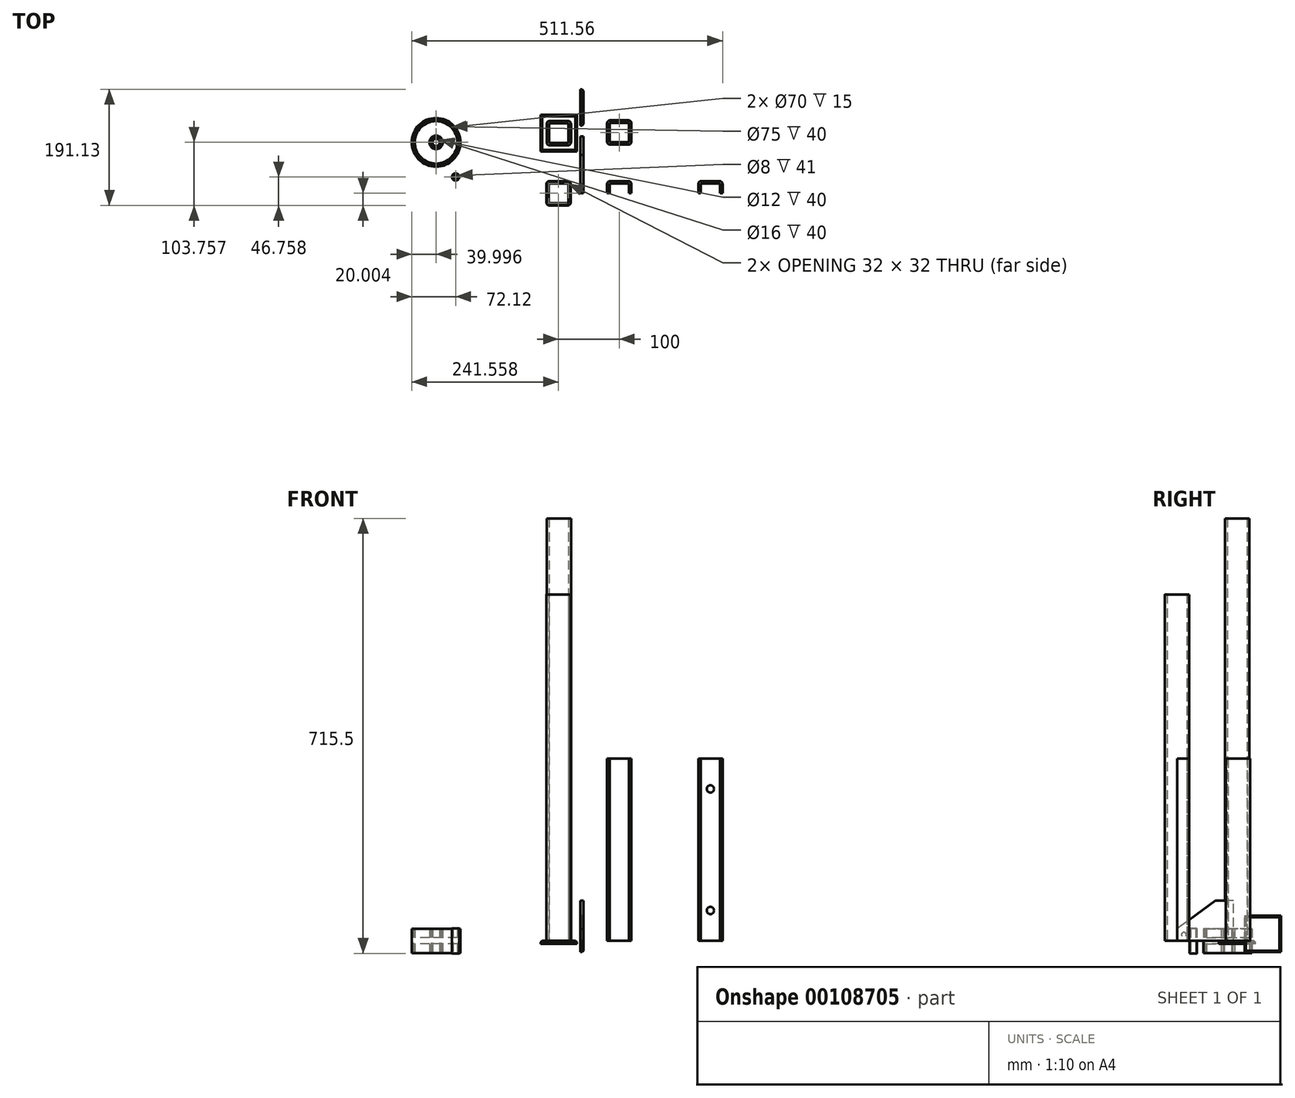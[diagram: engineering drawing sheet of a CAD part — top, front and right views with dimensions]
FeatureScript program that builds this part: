
annotation { "Feature Type Name" : "Feature", "Feature Type Description" : "" }
export const myFeature = defineFeature(function(context is Context, id is Id, definition is map)
    precondition{}
    {
        {
            var Q0;
            Q0=qCreatedBy(makeId("Top.planeOp"),FACE);
            var sketch = newSketch(context, id + "F0", { "sketchPlane" : qUnion([Q0])});
            skLineSegment(sketch, "E0.bottom", {"start": v(-50.42, 65.64) * mm, "end": v(-20.42, 65.64) * mm});
            skLineSegment(sketch, "E0.top", {"start": v(-50.42, 25.64) * mm, "end": v(-20.42, 25.64) * mm});
            skLineSegment(sketch, "E0.left", {"start": v(-55.42, 60.64) * mm, "end": v(-55.42, 30.64) * mm});
            skLineSegment(sketch, "E0.right", {"start": v(-15.42, 60.64) * mm, "end": v(-15.42, 30.64) * mm});
            skLineSegment(sketch, "E1.0", {"start": v(-51.42, 60.64) * mm, "end": v(-51.42, 30.64) * mm});
            skLineSegment(sketch, "E1.1", {"start": v(-50.42, 61.64) * mm, "end": v(-20.42, 61.64) * mm});
            skLineSegment(sketch, "E1.2", {"start": v(-19.42, 60.64) * mm, "end": v(-19.42, 30.64) * mm});
            skLineSegment(sketch, "E1.3", {"start": v(-50.42, 29.64) * mm, "end": v(-20.42, 29.64) * mm});
            skPoint(sketch, "E2.visualSharp", {"position": v(-51.42, 61.64) * mm});
            skArc(sketch, "E2.filletArc", {"start": v(-50.42, 61.64) * mm, "mid": v(-51.13, 61.35) * mm, "end": v(-51.42, 60.64) * mm});
            skPoint(sketch, "E3.visualSharp", {"position": v(-19.42, 61.64) * mm});
            skArc(sketch, "E3.filletArc", {"start": v(-19.42, 60.64) * mm, "mid": v(-19.71, 61.35) * mm, "end": v(-20.42, 61.64) * mm});
            skPoint(sketch, "E4.visualSharp", {"position": v(-19.42, 29.64) * mm});
            skArc(sketch, "E4.filletArc", {"start": v(-20.42, 29.64) * mm, "mid": v(-19.71, 29.93) * mm, "end": v(-19.42, 30.64) * mm});
            skPoint(sketch, "E5.visualSharp", {"position": v(-51.42, 29.64) * mm});
            skArc(sketch, "E5.filletArc", {"start": v(-51.42, 30.64) * mm, "mid": v(-51.13, 29.93) * mm, "end": v(-50.42, 29.64) * mm});
            skPoint(sketch, "E6.visualSharp", {"position": v(-55.42, 65.64) * mm});
            skArc(sketch, "E6.filletArc", {"start": v(-50.42, 65.64) * mm, "mid": v(-53.96, 64.17) * mm, "end": v(-55.42, 60.64) * mm});
            skPoint(sketch, "E7.visualSharp", {"position": v(-15.42, 65.64) * mm});
            skArc(sketch, "E7.filletArc", {"start": v(-15.42, 60.64) * mm, "mid": v(-16.88, 64.17) * mm, "end": v(-20.42, 65.64) * mm});
            skPoint(sketch, "E8.visualSharp", {"position": v(-15.42, 25.64) * mm});
            skArc(sketch, "E8.filletArc", {"start": v(-20.42, 25.64) * mm, "mid": v(-16.88, 27.1) * mm, "end": v(-15.42, 30.64) * mm});
            skLineSegment(sketch, "E9.0.1.0", {"start": v(-50.9, -69.37) * mm, "end": v(-20.9, -69.37) * mm});
            skLineSegment(sketch, "E9.0.1.1", {"start": v(-19.9, -38.37) * mm, "end": v(-19.9, -68.37) * mm});
            skPoint(sketch, "E9.0.1.2", {"position": v(-19.9, -37.37) * mm});
            skLineSegment(sketch, "E9.0.1.3", {"start": v(-50.9, -37.37) * mm, "end": v(-20.9, -37.37) * mm});
            skLineSegment(sketch, "E9.0.1.4", {"start": v(-50.9, -33.37) * mm, "end": v(-20.9, -33.37) * mm});
            skPoint(sketch, "E9.0.1.5", {"position": v(-51.9, -69.37) * mm});
            skPoint(sketch, "E9.0.1.6", {"position": v(-51.9, -37.37) * mm});
            skLineSegment(sketch, "E9.0.1.7", {"start": v(-50.9, -73.37) * mm, "end": v(-20.9, -73.37) * mm});
            skPoint(sketch, "E9.0.1.8", {"position": v(-19.9, -69.37) * mm});
            skLineSegment(sketch, "E9.0.1.9", {"start": v(-51.9, -38.37) * mm, "end": v(-51.9, -68.37) * mm});
            skLineSegment(sketch, "E9.0.1.10", {"start": v(-55.9, -38.37) * mm, "end": v(-55.9, -68.37) * mm});
            skLineSegment(sketch, "E9.0.1.11", {"start": v(-15.9, -38.37) * mm, "end": v(-15.9, -68.37) * mm});
            skPoint(sketch, "E9.0.1.12", {"position": v(-55.9, -33.37) * mm});
            skPoint(sketch, "E9.0.1.13", {"position": v(-15.9, -33.37) * mm});
            skPoint(sketch, "E9.0.1.14", {"position": v(-15.9, -73.37) * mm});
            skArc(sketch, "E9.0.1.15", {"start": v(-50.9, -33.37) * mm, "mid": v(-54.43, -34.83) * mm, "end": v(-55.9, -38.37) * mm});
            skArc(sketch, "E9.0.1.16", {"start": v(-20.9, -73.37) * mm, "mid": v(-17.36, -71.9) * mm, "end": v(-15.9, -68.37) * mm});
            skArc(sketch, "E9.0.1.17", {"start": v(-15.9, -38.37) * mm, "mid": v(-17.36, -34.83) * mm, "end": v(-20.9, -33.37) * mm});
            skArc(sketch, "E9.0.1.18", {"start": v(-19.9, -38.37) * mm, "mid": v(-20.19, -37.66) * mm, "end": v(-20.9, -37.37) * mm});
            skArc(sketch, "E9.0.1.19", {"start": v(-51.9, -68.37) * mm, "mid": v(-51.6, -69.07) * mm, "end": v(-50.9, -69.37) * mm});
            skArc(sketch, "E9.0.1.20", {"start": v(-50.9, -37.37) * mm, "mid": v(-51.6, -37.66) * mm, "end": v(-51.9, -38.37) * mm});
            skArc(sketch, "E9.0.1.21", {"start": v(-20.9, -69.37) * mm, "mid": v(-20.19, -69.07) * mm, "end": v(-19.9, -68.37) * mm});
            skLineSegment(sketch, "E9.1.0.0", {"start": v(49.1, 30.63) * mm, "end": v(79.1, 30.63) * mm});
            skLineSegment(sketch, "E9.1.0.1", {"start": v(80.1, 61.63) * mm, "end": v(80.1, 31.63) * mm});
            skPoint(sketch, "E9.1.0.2", {"position": v(80.1, 62.63) * mm});
            skLineSegment(sketch, "E9.1.0.3", {"start": v(49.1, 62.63) * mm, "end": v(79.1, 62.63) * mm});
            skLineSegment(sketch, "E9.1.0.4", {"start": v(49.1, 66.63) * mm, "end": v(79.1, 66.63) * mm});
            skPoint(sketch, "E9.1.0.5", {"position": v(48.1, 30.63) * mm});
            skPoint(sketch, "E9.1.0.6", {"position": v(48.1, 62.63) * mm});
            skLineSegment(sketch, "E9.1.0.7", {"start": v(49.1, 26.63) * mm, "end": v(79.1, 26.63) * mm});
            skPoint(sketch, "E9.1.0.8", {"position": v(80.1, 30.63) * mm});
            skLineSegment(sketch, "E9.1.0.9", {"start": v(48.1, 61.63) * mm, "end": v(48.1, 31.63) * mm});
            skLineSegment(sketch, "E9.1.0.10", {"start": v(44.1, 61.63) * mm, "end": v(44.1, 31.63) * mm});
            skLineSegment(sketch, "E9.1.0.11", {"start": v(84.1, 61.63) * mm, "end": v(84.1, 31.63) * mm});
            skPoint(sketch, "E9.1.0.12", {"position": v(44.1, 66.63) * mm});
            skPoint(sketch, "E9.1.0.13", {"position": v(84.1, 66.63) * mm});
            skPoint(sketch, "E9.1.0.14", {"position": v(84.1, 26.63) * mm});
            skArc(sketch, "E9.1.0.15", {"start": v(49.1, 66.63) * mm, "mid": v(45.57, 65.17) * mm, "end": v(44.1, 61.63) * mm});
            skArc(sketch, "E9.1.0.16", {"start": v(79.1, 26.63) * mm, "mid": v(82.64, 28.1) * mm, "end": v(84.1, 31.63) * mm});
            skArc(sketch, "E9.1.0.17", {"start": v(84.1, 61.63) * mm, "mid": v(82.64, 65.17) * mm, "end": v(79.1, 66.63) * mm});
            skArc(sketch, "E9.1.0.18", {"start": v(80.1, 61.63) * mm, "mid": v(79.81, 62.34) * mm, "end": v(79.1, 62.63) * mm});
            skArc(sketch, "E9.1.0.19", {"start": v(48.1, 31.63) * mm, "mid": v(48.4, 30.93) * mm, "end": v(49.1, 30.63) * mm});
            skArc(sketch, "E9.1.0.20", {"start": v(49.1, 62.63) * mm, "mid": v(48.4, 62.34) * mm, "end": v(48.1, 61.63) * mm});
            skArc(sketch, "E9.1.0.21", {"start": v(79.1, 30.63) * mm, "mid": v(79.81, 30.93) * mm, "end": v(80.1, 31.63) * mm});
            skPoint(sketch, "E9.1.1.2", {"position": v(80.1, -37.37) * mm});
            skLineSegment(sketch, "E9.1.1.3", {"start": v(49.1, -37.37) * mm, "end": v(79.1, -37.37) * mm});
            skLineSegment(sketch, "E9.1.1.4", {"start": v(49.1, -33.37) * mm, "end": v(79.1, -33.37) * mm});
            skPoint(sketch, "E9.1.1.6", {"position": v(48.1, -37.37) * mm});
            skLineSegment(sketch, "E9.1.1.9", {"start": v(48.1, -38.37) * mm, "end": v(48.1, -53.37) * mm});
            skPoint(sketch, "E9.1.1.12", {"position": v(44.1, -33.37) * mm});
            skPoint(sketch, "E9.1.1.13", {"position": v(84.1, -33.37) * mm});
            skArc(sketch, "E9.1.1.15", {"start": v(49.1, -33.37) * mm, "mid": v(45.57, -34.83) * mm, "end": v(44.1, -38.37) * mm});
            skArc(sketch, "E9.1.1.17", {"start": v(84.1, -38.37) * mm, "mid": v(82.64, -34.83) * mm, "end": v(79.1, -33.37) * mm});
            skArc(sketch, "E9.1.1.18", {"start": v(80.1, -38.37) * mm, "mid": v(79.81, -37.66) * mm, "end": v(79.1, -37.37) * mm});
            skArc(sketch, "E9.1.1.20", {"start": v(49.1, -37.37) * mm, "mid": v(48.4, -37.66) * mm, "end": v(48.1, -38.37) * mm});
            skPoint(sketch, "E10.visualSharp", {"position": v(-55.42, 25.64) * mm});
            skArc(sketch, "E10.filletArc", {"start": v(-55.42, 30.64) * mm, "mid": v(-53.96, 27.1) * mm, "end": v(-50.42, 25.64) * mm});
            skPoint(sketch, "E11.visualSharp", {"position": v(44.1, 26.63) * mm});
            skArc(sketch, "E11.filletArc", {"start": v(44.1, 31.63) * mm, "mid": v(45.57, 28.1) * mm, "end": v(49.1, 26.63) * mm});
            skPoint(sketch, "E12.visualSharp", {"position": v(-55.9, -73.37) * mm});
            skArc(sketch, "E12.filletArc", {"start": v(-55.9, -68.37) * mm, "mid": v(-54.43, -71.9) * mm, "end": v(-50.9, -73.37) * mm});
            skLineSegment(sketch, "E13", {"start": v(44.1, -53.37) * mm, "end": v(44.1, -38.37) * mm});
            skLineSegment(sketch, "E14", {"start": v(84.1, -38.37) * mm, "end": v(84.1, -53.37) * mm});
            skLineSegment(sketch, "E15", {"start": v(80.1, -38.37) * mm, "end": v(80.1, -53.37) * mm});
            skLineSegment(sketch, "E16", {"start": v(44.1, -53.37) * mm, "end": v(48.1, -53.37) * mm});
            skLineSegment(sketch, "E17", {"start": v(80.1, -53.37) * mm, "end": v(84.1, -53.37) * mm});
            skLineSegment(sketch, "E18.0", {"start": v(-20.42, 60.64) * mm, "end": v(-20.42, 30.64) * mm});
            skLineSegment(sketch, "E18.1", {"start": v(-50.42, 60.64) * mm, "end": v(-20.42, 60.64) * mm});
            skLineSegment(sketch, "E18.2", {"start": v(-50.42, 60.64) * mm, "end": v(-50.42, 30.64) * mm});
            skLineSegment(sketch, "E18.3", {"start": v(-50.42, 30.64) * mm, "end": v(-20.42, 30.64) * mm});
            skLineSegment(sketch, "E19.bottom", {"start": v(-65.42, 75.64) * mm, "end": v(-5.42, 75.64) * mm});
            skLineSegment(sketch, "E19.top", {"start": v(-65.42, 15.64) * mm, "end": v(-5.42, 15.64) * mm});
            skLineSegment(sketch, "E19.left", {"start": v(-65.42, 75.64) * mm, "end": v(-65.42, 15.64) * mm});
            skLineSegment(sketch, "E19.right", {"start": v(-5.42, 75.64) * mm, "end": v(-5.42, 15.64) * mm});
            skPoint(sketch, "E19.middle", {"position": v(-35.42, 45.64) * mm});
            skPoint(sketch, "E19.middle.positionSnap0", {"position": v(-20.42, 45.64) * mm});
            skPoint(sketch, "E19.middle.positionSnap1", {"position": v(-35.42, 30.64) * mm});
            skPoint(sketch, "E19.centerSnap0", {"position": v(-20.42, 45.64) * mm});
            skPoint(sketch, "E19.centerSnap1", {"position": v(-35.42, 30.64) * mm});
            skSolve(sketch);
        }
        {
            var Q0;
            Q0=qCreatedBy(makeId("Right.planeOp"),FACE);
            var sketch = newSketch(context, id + "F1", { "sketchPlane" : qUnion([Q0])});
            skLineSegment(sketch, "E20", {"start": v(-53.07, 0) * mm, "end": v(39.93, 0) * mm});
            skLineSegment(sketch, "E21", {"start": v(39.93, 0) * mm, "end": v(39.93, 66) * mm});
            skLineSegment(sketch, "E22", {"start": v(39.93, 66) * mm, "end": v(9.93, 66) * mm});
            skLineSegment(sketch, "E23", {"start": v(9.93, 66) * mm, "end": v(-53.07, 20.01) * mm});
            skLineSegment(sketch, "E24", {"start": v(-53.07, 20.01) * mm, "end": v(-53.07, 0) * mm});
            skLineSegment(sketch, "E25.bottom", {"start": v(57.76, 41.49) * mm, "end": v(117.76, 41.49) * mm});
            skLineSegment(sketch, "E25.top", {"start": v(57.76, -18.51) * mm, "end": v(117.76, -18.51) * mm});
            skLineSegment(sketch, "E25.left", {"start": v(57.76, 41.49) * mm, "end": v(57.76, -18.51) * mm});
            skLineSegment(sketch, "E25.right", {"start": v(117.76, 41.49) * mm, "end": v(117.76, -18.51) * mm});
            skCircle(sketch, "E26", {"center": v(-42.07, 10) * mm, "radius": 4 * mm});
            skSolve(sketch);
        }
        {
            var Q0;
            Q0=makeQuery(id+"F0.imprint","IMPRINT",FACE,{"disambiguationData":[TD([[makeQuery(id+"F0.imprint","IMPRINT",EDGE,{"derivedFrom":sQuery(id+"F0.wireOp",EDGE,"E0.bottom")}),-1.0]])]});
            extrude(context, id + "F2", {"entities" : qUnion([Q0]), "depth" : 695 * mm});
        }
        {
            var Q0;
            Q0=makeQuery(id+"F0.imprint","IMPRINT",FACE,{"disambiguationData":[TD([[makeQuery(id+"F0.imprint","IMPRINT",EDGE,{"derivedFrom":sQuery(id+"F0.wireOp",EDGE,"E9.0.1.0")}),-1.0]])]});
            extrude(context, id + "F3", {"entities" : qUnion([Q0]), "depth" : 570 * mm});
        }
        {
            var Q0;
            Q0=makeQuery(id+"F0.imprint","IMPRINT",FACE,{"disambiguationData":[TD([[makeQuery(id+"F0.imprint","IMPRINT",EDGE,{"derivedFrom":sQuery(id+"F0.wireOp",EDGE,"E9.1.0.0")}),-1.0]])]});
            extrude(context, id + "F4", {"entities" : qUnion([Q0]), "depth" : 300 * mm});
        }
        {
            var Q0;
            Q0=makeQuery(id+"F0.imprint","IMPRINT",FACE,{"disambiguationData":[TD([[makeQuery(id+"F0.imprint","IMPRINT",EDGE,{"derivedFrom":sQuery(id+"F0.wireOp",EDGE,"E9.1.1.3")}),1.0]])]});
            extrude(context, id + "F5", {"entities" : qUnion([Q0]), "depth" : 300 * mm});
        }
        {
            var Q0;
            Q0=makeQuery(id+"F1.imprint","IMPRINT",FACE,{"disambiguationData":[TD([[makeQuery(id+"F1.imprint","IMPRINT",EDGE,{"derivedFrom":sQuery(id+"F1.wireOp",EDGE,"E20")}),1.0]])]});
            var Q1;
            Q1=makeQuery(id+"F1.imprint","IMPRINT",FACE,{"disambiguationData":[TD([[makeQuery(id+"F1.imprint","IMPRINT",EDGE,{"derivedFrom":sQuery(id+"F1.wireOp",EDGE,"E25.bottom")}),-1.0]])]});
            extrude(context, id + "F6", {"entities" : qUnion([Q0, Q1]), "depth" : 5 * mm});
        }
        {
            var Q0;
            Q0=makeQuery(id+"F6.opExtrude","CAP_EDGE",EDGE,{"disambiguationData":[OSD([sQuery(id+"F1.wireOp",EDGE,"E25.bottom")])],"isStart":false});
            var Q1;
            Q1=makeQuery(id+"F6.opExtrude","CAP_EDGE",EDGE,{"disambiguationData":[OSD([sQuery(id+"F1.wireOp",EDGE,"E25.right")])],"isStart":false});
            var Q2;
            Q2=makeQuery(id+"F6.opExtrude","CAP_EDGE",EDGE,{"disambiguationData":[OSD([sQuery(id+"F1.wireOp",EDGE,"E25.left")])],"isStart":false});
            var Q3;
            Q3=makeQuery(id+"F6.opExtrude","CAP_EDGE",EDGE,{"disambiguationData":[OSD([sQuery(id+"F1.wireOp",EDGE,"E25.top")])],"isStart":false});
            chamfer(context, id + "F7", {"entities" : qUnion([Q0, Q1, Q2, Q3]), "width" : 2.5 * mm, "tangentPropagation" : true});
        }
        {
            var Q0;
            Q0=makeQuery(id+"F5.opExtrude","SWEPT_BODY",BODY,{"disambiguationData":[OSD([sQuery(id+"F0.wireOp",EDGE,"E9.1.1.3"),sQuery(id+"F0.wireOp",EDGE,"E9.1.1.4"),sQuery(id+"F0.wireOp",EDGE,"E9.1.1.9"),sQuery(id+"F0.wireOp",EDGE,"E9.1.1.15"),sQuery(id+"F0.wireOp",EDGE,"E9.1.1.17"),sQuery(id+"F0.wireOp",EDGE,"E9.1.1.18"),sQuery(id+"F0.wireOp",EDGE,"E9.1.1.20"),sQuery(id+"F0.wireOp",EDGE,"E13"),sQuery(id+"F0.wireOp",EDGE,"E14"),sQuery(id+"F0.wireOp",EDGE,"E15"),sQuery(id+"F0.wireOp",EDGE,"E16"),sQuery(id+"F0.wireOp",EDGE,"E17")])]});
            transform(context, id + "F8", {"entities" : qUnion([Q0]), "transformType" : TransformType.TRANSLATION_3D, "dx" : 150 * mm, "dy" : 0 * mm, "dz" : 0 * mm, "makeCopy" : true});
        }
        {
            var Q0;
            Q0=makeQuery(id+"F8.opPattern","COPY",FACE,{"derivedFrom":makeQuery(id+"F5.opExtrude","SWEPT_FACE",FACE,{"disambiguationData":[OSD([sQuery(id+"F0.wireOp",EDGE,"E9.1.1.4")])]}),"instanceName":"1"});
            var sketch = newSketch(context, id + "F9", { "sketchPlane" : qUnion([Q0])});
            skLineSegment(sketch, "E27", {"start": v(-214.1, 250) * mm, "end": v(-214.1, 50) * mm, "construction": true});
            skSolve(sketch);
        }
        {
            var Q0;
            Q0=sQuery(id+"F9.wireOp",VERTEX,"E27.end");
            var Q1;
            Q1=sQuery(id+"F9.wireOp",VERTEX,"E27.start");
            var Q2;
            Q2=makeQuery(id+"F8.opPattern","COPY",BODY,{"derivedFrom":makeQuery(id+"F5.opExtrude","SWEPT_BODY",BODY,{"disambiguationData":[OSD([sQuery(id+"F0.wireOp",EDGE,"E9.1.1.3"),sQuery(id+"F0.wireOp",EDGE,"E9.1.1.4"),sQuery(id+"F0.wireOp",EDGE,"E9.1.1.9"),sQuery(id+"F0.wireOp",EDGE,"E9.1.1.15"),sQuery(id+"F0.wireOp",EDGE,"E9.1.1.17"),sQuery(id+"F0.wireOp",EDGE,"E9.1.1.18"),sQuery(id+"F0.wireOp",EDGE,"E9.1.1.20"),sQuery(id+"F0.wireOp",EDGE,"E13"),sQuery(id+"F0.wireOp",EDGE,"E14"),sQuery(id+"F0.wireOp",EDGE,"E15"),sQuery(id+"F0.wireOp",EDGE,"E16"),sQuery(id+"F0.wireOp",EDGE,"E17")])]}),"instanceName":"1"});
            hole(context, id + "F10", {"style" : HoleStyle.SIMPLE, "endStyle" : HoleEndStyle.THROUGH, "holeDiameter" : 12 * mm, "locations" : qUnion([Q0, Q1]), "scope" : qUnion([Q2]), "isTappedThrough" : true});
        }
        {
            var Q0;
            Q0=makeQuery(id+"F0.imprint","IMPRINT",FACE,{"disambiguationData":[TD([[makeQuery(id+"F0.imprint","IMPRINT",EDGE,{"derivedFrom":sQuery(id+"F0.wireOp",EDGE,"E0.bottom")}),1.0]])]});
            var Q1;
            Q1=makeQuery(id+"F0.imprint","IMPRINT",FACE,{"disambiguationData":[TD([[makeQuery(id+"F0.imprint","IMPRINT",EDGE,{"derivedFrom":sQuery(id+"F0.wireOp",EDGE,"E0.bottom")}),-1.0]])]});
            var Q2;
            Q2=makeQuery(id+"F0.imprint","IMPRINT",FACE,{"disambiguationData":[TD([[makeQuery(id+"F0.imprint","IMPRINT",EDGE,{"derivedFrom":sQuery(id+"F0.wireOp",EDGE,"E18.0")}),-1.0]])]});
            var Q3;
            Q3=makeQuery(id+"F0.imprint","IMPRINT",FACE,{"disambiguationData":[TD([[makeQuery(id+"F0.imprint","IMPRINT",EDGE,{"derivedFrom":sQuery(id+"F0.wireOp",EDGE,"E1.0")}),1.0]])]});
            extrude(context, id + "F11", {"entities" : qUnion([Q0, Q1, Q2, Q3]), "operationType" : NewBodyOperationType.ADD, "oppositeDirection" : true, "depth" : 5 * mm});
        }
        {
            var Q0;
            Q0=makeQuery(id+"F11.opExtrude","CAP_EDGE",EDGE,{"disambiguationData":[OSD([sQuery(id+"F0.wireOp",EDGE,"E19.right")])],"isStart":true});
            var Q1;
            Q1=makeQuery(id+"F11.opExtrude","CAP_EDGE",EDGE,{"disambiguationData":[OSD([sQuery(id+"F0.wireOp",EDGE,"E19.top")])],"isStart":true});
            var Q2;
            Q2=makeQuery(id+"F11.opExtrude","CAP_EDGE",EDGE,{"disambiguationData":[OSD([sQuery(id+"F0.wireOp",EDGE,"E19.bottom")])],"isStart":true});
            var Q3;
            Q3=makeQuery(id+"F11.opExtrude","CAP_EDGE",EDGE,{"disambiguationData":[OSD([sQuery(id+"F0.wireOp",EDGE,"E19.left")])],"isStart":true});
            chamfer(context, id + "F12", {"entities" : qUnion([Q0, Q1, Q2, Q3]), "width" : 2.5 * mm, "tangentPropagation" : true});
        }
        {
            var Q0;
            Q0=qCreatedBy(makeId("Top.planeOp"),FACE);
            var sketch = newSketch(context, id + "F13", { "sketchPlane" : qUnion([Q0])});
            skCircle(sketch, "E28", {"center": v(-237.45, 30.39) * mm, "radius": 40 * mm});
            skCircle(sketch, "E29", {"center": v(-237.45, 30.39) * mm, "radius": 6 * mm});
            skCircle(sketch, "E30", {"center": v(-237.45, 30.39) * mm, "radius": 37.5 * mm});
            skCircle(sketch, "E31", {"center": v(-237.45, 30.39) * mm, "radius": 35 * mm});
            skCircle(sketch, "E32", {"center": v(-237.45, 30.39) * mm, "radius": 8 * mm});
            skCircle(sketch, "E33", {"center": v(-237.45, 30.39) * mm, "radius": 11 * mm});
            skCircle(sketch, "E34", {"center": v(-205.33, -26.61) * mm, "radius": 6 * mm});
            skCircle(sketch, "E35", {"center": v(-205.33, -26.61) * mm, "radius": 4 * mm});
            skSolve(sketch);
        }
        {
            var Q0;
            Q0=makeQuery(id+"F13.imprint","IMPRINT",FACE,{"disambiguationData":[TD([[makeQuery(id+"F13.imprint","IMPRINT",EDGE,{"derivedFrom":sQuery(id+"F13.wireOp",EDGE,"E29")}),-1.0]])]});
            extrude(context, id + "F14", {"entities" : qUnion([Q0]), "endBound" : BoundingType.SYMMETRIC, "depth" : 40 * mm});
        }
        {
            var Q0;
            Q0=makeQuery(id+"F13.imprint","IMPRINT",FACE,{"disambiguationData":[TD([[makeQuery(id+"F13.imprint","IMPRINT",EDGE,{"derivedFrom":sQuery(id+"F13.wireOp",EDGE,"E32")}),-1.0]])]});
            extrude(context, id + "F15", {"entities" : qUnion([Q0]), "endBound" : BoundingType.SYMMETRIC, "depth" : 40 * mm});
        }
        {
            var Q0;
            Q0=makeQuery(id+"F13.imprint","IMPRINT",FACE,{"disambiguationData":[TD([[makeQuery(id+"F13.imprint","IMPRINT",EDGE,{"derivedFrom":sQuery(id+"F13.wireOp",EDGE,"E31")}),1.0]])]});
            extrude(context, id + "F16", {"entities" : qUnion([Q0]), "operationType" : NewBodyOperationType.ADD, "endBound" : BoundingType.SYMMETRIC, "depth" : 10 * mm});
        }
        {
            var Q0;
            Q0=makeQuery(id+"F13.imprint","IMPRINT",FACE,{"disambiguationData":[TD([[makeQuery(id+"F13.imprint","IMPRINT",EDGE,{"derivedFrom":sQuery(id+"F13.wireOp",EDGE,"E30")}),1.0]])]});
            extrude(context, id + "F17", {"entities" : qUnion([Q0]), "operationType" : NewBodyOperationType.ADD, "endBound" : BoundingType.SYMMETRIC, "depth" : 40 * mm});
        }
        {
            var Q0;
            Q0=makeQuery(id+"F13.imprint","IMPRINT",FACE,{"disambiguationData":[TD([[makeQuery(id+"F13.imprint","IMPRINT",EDGE,{"derivedFrom":sQuery(id+"F13.wireOp",EDGE,"E28")}),1.0]])]});
            extrude(context, id + "F18", {"entities" : qUnion([Q0]), "endBound" : BoundingType.SYMMETRIC, "depth" : 40 * mm});
        }
        {
            var Q0;
            Q0=makeQuery(id+"F13.imprint","IMPRINT",FACE,{"disambiguationData":[TD([[makeQuery(id+"F13.imprint","IMPRINT",EDGE,{"derivedFrom":sQuery(id+"F13.wireOp",EDGE,"E34")}),1.0]])]});
            extrude(context, id + "F19", {"entities" : qUnion([Q0]), "endBound" : BoundingType.SYMMETRIC, "depth" : 41 * mm});
        }
    });
